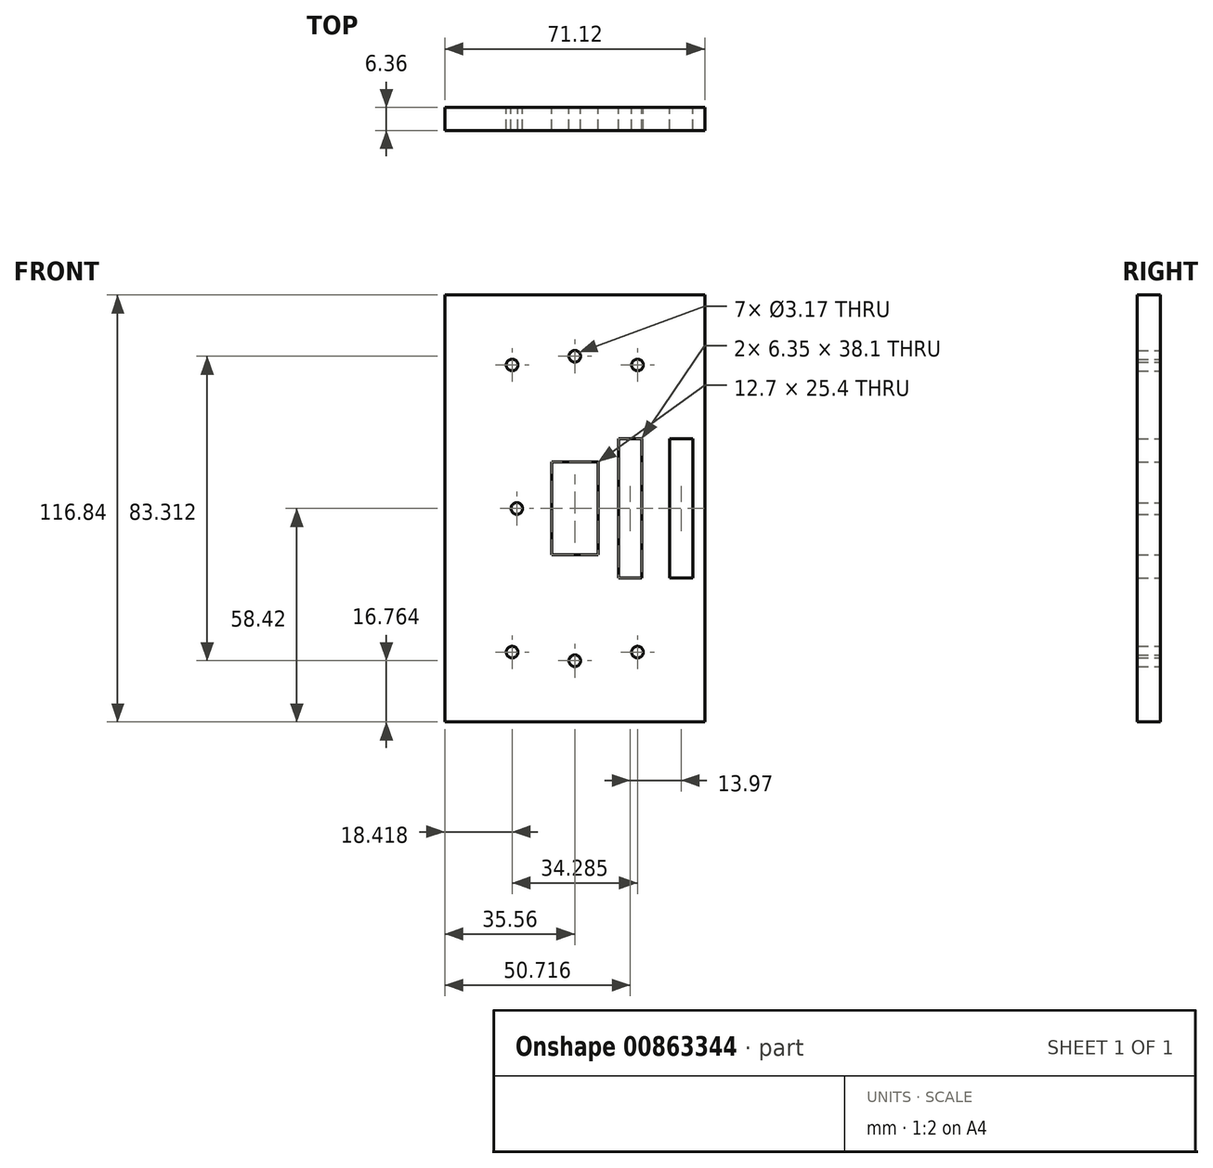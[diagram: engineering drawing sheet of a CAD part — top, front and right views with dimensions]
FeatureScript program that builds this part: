
annotation { "Feature Type Name" : "Feature", "Feature Type Description" : "" }
export const myFeature = defineFeature(function(context is Context, id is Id, definition is map)
    precondition{}
    {
        {
            var Q0;
            Q0=qCreatedBy(makeId("Front.planeOp"),FACE);
            var sketch = newSketch(context, id + "F0", { "sketchPlane" : qUnion([Q0])});
            skLineSegment(sketch, "E0.bottom", {"start": v(35.56, 58.42) * mm, "end": v(-35.56, 58.42) * mm});
            skLineSegment(sketch, "E0.top", {"start": v(35.56, -58.42) * mm, "end": v(-35.56, -58.42) * mm});
            skLineSegment(sketch, "E0.left", {"start": v(35.56, 58.42) * mm, "end": v(35.56, -58.42) * mm});
            skLineSegment(sketch, "E0.right", {"start": v(-35.56, 58.42) * mm, "end": v(-35.56, -58.42) * mm});
            skPoint(sketch, "E0.middle", {"position": v(0, 0) * mm});
            skLineSegment(sketch, "E1.bottom", {"start": v(-6.35, 12.7) * mm, "end": v(6.35, 12.7) * mm});
            skLineSegment(sketch, "E1.top", {"start": v(-6.35, -12.7) * mm, "end": v(6.35, -12.7) * mm});
            skLineSegment(sketch, "E1.left", {"start": v(-6.35, 12.7) * mm, "end": v(-6.35, -12.7) * mm});
            skCircle(sketch, "E2", {"center": v(-17.14, 39.29) * mm, "radius": 1.59 * mm});
            skCircle(sketch, "E3.MirrorC", {"center": v(17.14, 39.29) * mm, "radius": 1.59 * mm});
            skCircle(sketch, "E4.MirrorC", {"center": v(-17.14, -39.29) * mm, "radius": 1.59 * mm});
            skCircle(sketch, "E5.MirrorC", {"center": v(17.14, -39.29) * mm, "radius": 1.59 * mm});
            skLineSegment(sketch, "E6", {"start": v(-15.85, 0) * mm, "end": v(-101.5, 0) * mm});
            skPoint(sketch, "E6.startSnap0", {"position": v(-6.35, 0) * mm});
            skCircle(sketch, "E7", {"center": v(-15.85, 0) * mm, "radius": 1.59 * mm});
            skLineSegment(sketch, "E8", {"start": v(6.35, 12.7) * mm, "end": v(6.35, -12.7) * mm});
            skPoint(sketch, "E9.middle", {"position": v(9.99, 0) * mm});
            skLineSegment(sketch, "E10", {"start": v(0, 12.7) * mm, "end": v(0, 41.66) * mm});
            skCircle(sketch, "E11", {"center": v(0, 41.66) * mm, "radius": 1.59 * mm});
            skCircle(sketch, "E12.MirrorC", {"center": v(0, -41.66) * mm, "radius": 1.59 * mm});
            skLineSegment(sketch, "E13.bottom", {"start": v(32.3, 19.05) * mm, "end": v(25.95, 19.05) * mm});
            skLineSegment(sketch, "E13.top", {"start": v(32.3, -19.05) * mm, "end": v(25.95, -19.05) * mm});
            skLineSegment(sketch, "E13.left", {"start": v(32.3, 19.05) * mm, "end": v(32.3, -19.05) * mm});
            skLineSegment(sketch, "E13.right", {"start": v(25.95, 19.05) * mm, "end": v(25.95, -19.05) * mm});
            skPoint(sketch, "E13.middle", {"position": v(29.13, 0) * mm});
            skLineSegment(sketch, "E14", {"start": v(22.14, 0) * mm, "end": v(22.14, 29.1) * mm});
            skLineSegment(sketch, "E15.MirrorCS", {"start": v(18.33, 19.05) * mm, "end": v(18.33, -19.05) * mm});
            skLineSegment(sketch, "E16.MirrorCS", {"start": v(11.98, 19.05) * mm, "end": v(18.33, 19.05) * mm});
            skLineSegment(sketch, "E17.MirrorCS", {"start": v(11.98, 19.05) * mm, "end": v(11.98, -19.05) * mm});
            skLineSegment(sketch, "E18.MirrorCS", {"start": v(11.98, -19.05) * mm, "end": v(18.33, -19.05) * mm});
            skSolve(sketch);
        }
        {
            var Q0;
            Q0=makeQuery(id+"F0.imprint","IMPRINT",FACE,{"disambiguationData":[TD([[makeQuery(id+"F0.imprint","IMPRINT",EDGE,{"derivedFrom":sQuery(id+"F0.wireOp",EDGE,"E0.bottom")}),1.0]])]});
            var Q1;
            {var subQ0=sQuery(id+"F0.wireOp",EDGE,"02456610-d92d-464a-957a-78d5448d8da0.0");Q1=makeQuery(id+"F0.imprint","IMPRINT",FACE,{"disambiguationData":[TD([[makeQuery(id+"F0.imprint","IMPRINT",EDGE,{"derivedFrom":subQ0}),-1.0]])]});}
            extrude(context, id + "F1", {"entities" : qUnion([Q0, Q1]), "endBound" : BoundingType.SYMMETRIC, "depth" : 6.35 * mm, "offsetDistance" : 25 * mm});
        }
        {
            var Q0;
            Q0=makeQuery(id+"F0.imprint","IMPRINT",FACE,{"disambiguationData":[TD([[makeQuery(id+"F0.imprint","IMPRINT",EDGE,{"derivedFrom":sQuery(id+"F0.wireOp",EDGE,"E15.MirrorCS")}),-1.0]])]});
            var Q1;
            Q1=makeQuery(id+"F0.imprint","IMPRINT",FACE,{"disambiguationData":[TD([[makeQuery(id+"F0.imprint","IMPRINT",EDGE,{"derivedFrom":sQuery(id+"F0.wireOp",EDGE,"E13.bottom")}),1.0]])]});
            extrude(context, id + "F2", {"entities" : qUnion([Q0, Q1]), "operationType" : NewBodyOperationType.REMOVE, "oppositeDirection" : true, "depth" : 2.54 * mm, "offsetDistance" : 25.4 * mm});
        }
    });
